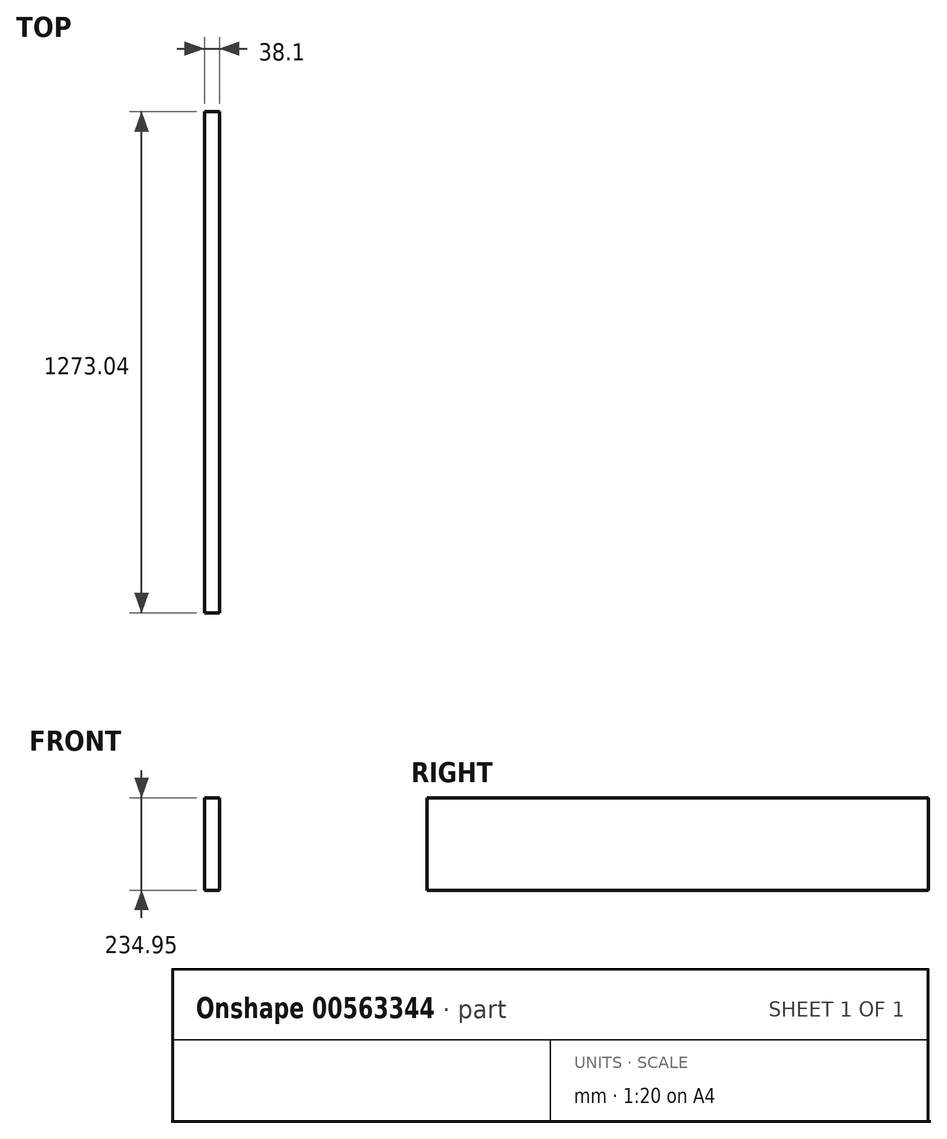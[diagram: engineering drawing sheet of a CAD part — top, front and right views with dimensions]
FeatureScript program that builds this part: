
annotation { "Feature Type Name" : "Feature", "Feature Type Description" : "" }
export const myFeature = defineFeature(function(context is Context, id is Id, definition is map)
    precondition{}
    {
        {
            var Q0;
            Q0=qCreatedBy(makeId("Top.planeOp"),FACE);
            var sketch = newSketch(context, id + "F0", { "sketchPlane" : qUnion([Q0])});
            skLineSegment(sketch, "E0.bottom", {"start": v(-19.05, -636.52) * mm, "end": v(19.05, -636.52) * mm});
            skLineSegment(sketch, "E0.top", {"start": v(-19.05, 636.52) * mm, "end": v(19.05, 636.52) * mm});
            skLineSegment(sketch, "E0.left", {"start": v(-19.05, -636.52) * mm, "end": v(-19.05, 636.52) * mm});
            skLineSegment(sketch, "E0.right", {"start": v(19.05, -636.52) * mm, "end": v(19.05, 636.52) * mm});
            skPoint(sketch, "E0.middle", {"position": v(0, 0) * mm});
            skSolve(sketch);
        }
        {
            var Q0;
            Q0 = qSketchRegion(id + "F0", true);
            extrude(context, id + "F1", {"entities" : qUnion([Q0]), "depth" : 234.95 * mm, "offsetDistance" : 25.4 * mm});
        }
    });
